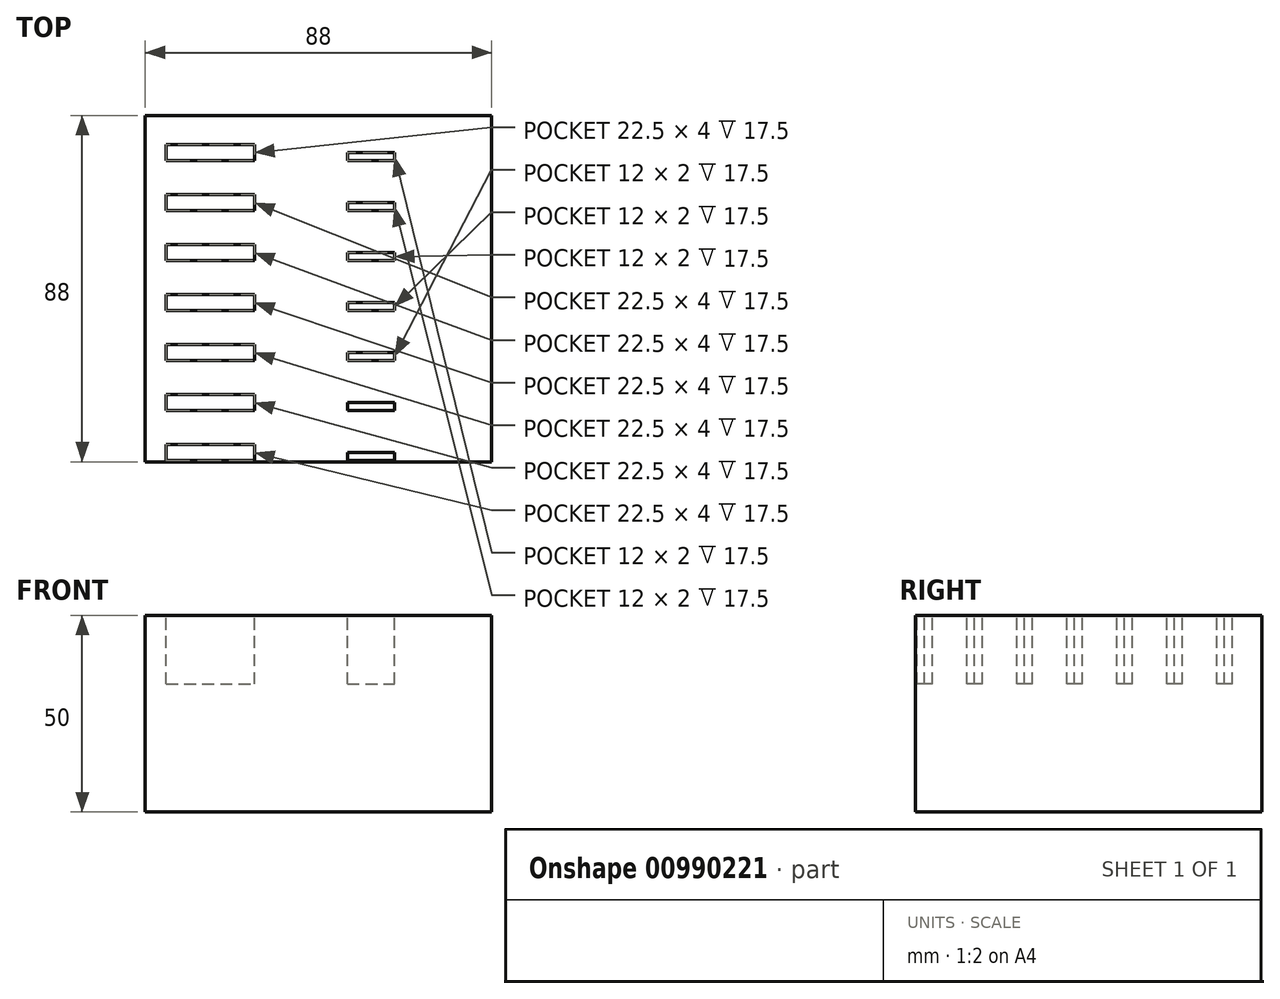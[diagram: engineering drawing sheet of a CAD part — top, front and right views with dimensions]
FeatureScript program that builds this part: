
annotation { "Feature Type Name" : "Feature", "Feature Type Description" : "" }
export const myFeature = defineFeature(function(context is Context, id is Id, definition is map)
    precondition{}
    {
        {
            var Q0;
            Q0=qCreatedBy(makeId("Top.planeOp"),FACE);
            var sketch = newSketch(context, id + "F0", { "sketchPlane" : qUnion([Q0])});
            skLineSegment(sketch, "E0.bottom", {"start": v(-39.99, 39.28) * mm, "end": v(48.01, 39.28) * mm});
            skLineSegment(sketch, "E0.top", {"start": v(-39.99, -48.72) * mm, "end": v(48.01, -48.72) * mm});
            skLineSegment(sketch, "E0.left", {"start": v(-39.99, 39.28) * mm, "end": v(-39.99, -48.72) * mm});
            skLineSegment(sketch, "E0.right", {"start": v(48.01, 39.28) * mm, "end": v(48.01, -48.72) * mm});
            skSolve(sketch);
        }
        {
            var Q0;
            Q0 = qSketchRegion(id + "F0", true);
            extrude(context, id + "F1", {"entities" : qUnion([Q0]), "depth" : 50 * mm, "offsetDistance" : 25.4 * mm});
        }
        {
            var Q0;
            Q0=makeQuery(id+"F1.opExtrude","CAP_FACE",FACE,{"disambiguationData":[OSD([sQuery(id+"F0.wireOp",EDGE,"E0.bottom"),sQuery(id+"F0.wireOp",EDGE,"E0.top"),sQuery(id+"F0.wireOp",EDGE,"E0.left"),sQuery(id+"F0.wireOp",EDGE,"E0.right")])],"isStart":false});
            var sketch = newSketch(context, id + "F2", { "sketchPlane" : qUnion([Q0])});
            skLineSegment(sketch, "E1.bottom", {"start": v(-34.7, 31.81) * mm, "end": v(-12.2, 31.81) * mm});
            skLineSegment(sketch, "E1.top", {"start": v(-34.7, 27.81) * mm, "end": v(-12.2, 27.81) * mm});
            skLineSegment(sketch, "E1.left", {"start": v(-34.7, 31.81) * mm, "end": v(-34.7, 27.81) * mm});
            skLineSegment(sketch, "E1.right", {"start": v(-12.2, 31.81) * mm, "end": v(-12.2, 27.81) * mm});
            skLineSegment(sketch, "E2.0.1.0", {"start": v(-34.7, 15.11) * mm, "end": v(-12.2, 15.11) * mm});
            skLineSegment(sketch, "E2.0.1.1", {"start": v(-34.7, 19.11) * mm, "end": v(-34.7, 15.11) * mm});
            skLineSegment(sketch, "E2.0.1.2", {"start": v(-34.7, 19.11) * mm, "end": v(-12.2, 19.11) * mm});
            skLineSegment(sketch, "E2.0.1.3", {"start": v(-12.2, 19.11) * mm, "end": v(-12.2, 15.11) * mm});
            skLineSegment(sketch, "E2.0.2.0", {"start": v(-34.7, 2.41) * mm, "end": v(-12.2, 2.41) * mm});
            skLineSegment(sketch, "E2.0.2.1", {"start": v(-34.7, 6.41) * mm, "end": v(-34.7, 2.41) * mm});
            skLineSegment(sketch, "E2.0.2.2", {"start": v(-34.7, 6.41) * mm, "end": v(-12.2, 6.41) * mm});
            skLineSegment(sketch, "E2.0.2.3", {"start": v(-12.2, 6.41) * mm, "end": v(-12.2, 2.41) * mm});
            skLineSegment(sketch, "E2.0.3.0", {"start": v(-34.7, -10.29) * mm, "end": v(-12.2, -10.29) * mm});
            skLineSegment(sketch, "E2.0.3.1", {"start": v(-34.7, -6.29) * mm, "end": v(-34.7, -10.29) * mm});
            skLineSegment(sketch, "E2.0.3.2", {"start": v(-34.7, -6.29) * mm, "end": v(-12.2, -6.29) * mm});
            skLineSegment(sketch, "E2.0.3.3", {"start": v(-12.2, -6.29) * mm, "end": v(-12.2, -10.29) * mm});
            skLineSegment(sketch, "E2.0.4.0", {"start": v(-34.7, -22.99) * mm, "end": v(-12.2, -22.99) * mm});
            skLineSegment(sketch, "E2.0.4.1", {"start": v(-34.7, -18.99) * mm, "end": v(-34.7, -22.99) * mm});
            skLineSegment(sketch, "E2.0.4.2", {"start": v(-34.7, -18.99) * mm, "end": v(-12.2, -18.99) * mm});
            skLineSegment(sketch, "E2.0.4.3", {"start": v(-12.2, -18.99) * mm, "end": v(-12.2, -22.99) * mm});
            skLineSegment(sketch, "E2.0.5.0", {"start": v(-34.7, -35.69) * mm, "end": v(-12.2, -35.69) * mm});
            skLineSegment(sketch, "E2.0.5.1", {"start": v(-34.7, -31.69) * mm, "end": v(-34.7, -35.69) * mm});
            skLineSegment(sketch, "E2.0.5.2", {"start": v(-34.7, -31.69) * mm, "end": v(-12.2, -31.69) * mm});
            skLineSegment(sketch, "E2.0.5.3", {"start": v(-12.2, -31.69) * mm, "end": v(-12.2, -35.69) * mm});
            skLineSegment(sketch, "E2.0.6.0", {"start": v(-34.7, -48.39) * mm, "end": v(-12.2, -48.39) * mm});
            skLineSegment(sketch, "E2.0.6.1", {"start": v(-34.7, -44.39) * mm, "end": v(-34.7, -48.39) * mm});
            skLineSegment(sketch, "E2.0.6.2", {"start": v(-34.7, -44.39) * mm, "end": v(-12.2, -44.39) * mm});
            skLineSegment(sketch, "E2.0.6.3", {"start": v(-12.2, -44.39) * mm, "end": v(-12.2, -48.39) * mm});
            skLineSegment(sketch, "E2.1.1.0", {"start": v(-34.7, 15.11) * mm, "end": v(-12.2, 15.11) * mm});
            skLineSegment(sketch, "E2.1.1.1", {"start": v(-34.7, 19.11) * mm, "end": v(-34.7, 15.11) * mm});
            skLineSegment(sketch, "E2.1.1.2", {"start": v(-34.7, 19.11) * mm, "end": v(-12.2, 19.11) * mm});
            skLineSegment(sketch, "E2.1.1.3", {"start": v(-12.2, 19.11) * mm, "end": v(-12.2, 15.11) * mm});
            skLineSegment(sketch, "E2.1.2.0", {"start": v(-34.7, 2.41) * mm, "end": v(-12.2, 2.41) * mm});
            skLineSegment(sketch, "E2.1.2.1", {"start": v(-34.7, 6.41) * mm, "end": v(-34.7, 2.41) * mm});
            skLineSegment(sketch, "E2.1.2.2", {"start": v(-34.7, 6.41) * mm, "end": v(-12.2, 6.41) * mm});
            skLineSegment(sketch, "E2.1.2.3", {"start": v(-12.2, 6.41) * mm, "end": v(-12.2, 2.41) * mm});
            skLineSegment(sketch, "E2.1.3.0", {"start": v(-34.7, -10.29) * mm, "end": v(-12.2, -10.29) * mm});
            skLineSegment(sketch, "E2.1.3.1", {"start": v(-34.7, -6.29) * mm, "end": v(-34.7, -10.29) * mm});
            skLineSegment(sketch, "E2.1.3.2", {"start": v(-34.7, -6.29) * mm, "end": v(-12.2, -6.29) * mm});
            skLineSegment(sketch, "E2.1.3.3", {"start": v(-12.2, -6.29) * mm, "end": v(-12.2, -10.29) * mm});
            skLineSegment(sketch, "E2.1.4.0", {"start": v(-34.7, -22.99) * mm, "end": v(-12.2, -22.99) * mm});
            skLineSegment(sketch, "E2.1.4.1", {"start": v(-34.7, -18.99) * mm, "end": v(-34.7, -22.99) * mm});
            skLineSegment(sketch, "E2.1.4.2", {"start": v(-34.7, -18.99) * mm, "end": v(-12.2, -18.99) * mm});
            skLineSegment(sketch, "E2.1.4.3", {"start": v(-12.2, -18.99) * mm, "end": v(-12.2, -22.99) * mm});
            skLineSegment(sketch, "E2.1.5.0", {"start": v(-34.7, -35.69) * mm, "end": v(-12.2, -35.69) * mm});
            skLineSegment(sketch, "E2.1.5.1", {"start": v(-34.7, -31.69) * mm, "end": v(-34.7, -35.69) * mm});
            skLineSegment(sketch, "E2.1.5.2", {"start": v(-34.7, -31.69) * mm, "end": v(-12.2, -31.69) * mm});
            skLineSegment(sketch, "E2.1.5.3", {"start": v(-12.2, -31.69) * mm, "end": v(-12.2, -35.69) * mm});
            skLineSegment(sketch, "E2.1.6.0", {"start": v(-34.7, -48.39) * mm, "end": v(-12.2, -48.39) * mm});
            skLineSegment(sketch, "E2.1.6.1", {"start": v(-34.7, -44.39) * mm, "end": v(-34.7, -48.39) * mm});
            skLineSegment(sketch, "E2.1.6.2", {"start": v(-34.7, -44.39) * mm, "end": v(-12.2, -44.39) * mm});
            skLineSegment(sketch, "E2.1.6.3", {"start": v(-12.2, -44.39) * mm, "end": v(-12.2, -48.39) * mm});
            skLineSegment(sketch, "E2.2.1.0", {"start": v(-34.7, 15.11) * mm, "end": v(-12.2, 15.11) * mm});
            skLineSegment(sketch, "E2.2.1.1", {"start": v(-34.7, 19.11) * mm, "end": v(-34.7, 15.11) * mm});
            skLineSegment(sketch, "E2.2.1.2", {"start": v(-34.7, 19.11) * mm, "end": v(-12.2, 19.11) * mm});
            skLineSegment(sketch, "E2.2.1.3", {"start": v(-12.2, 19.11) * mm, "end": v(-12.2, 15.11) * mm});
            skLineSegment(sketch, "E2.2.2.0", {"start": v(-34.7, 2.41) * mm, "end": v(-12.2, 2.41) * mm});
            skLineSegment(sketch, "E2.2.2.1", {"start": v(-34.7, 6.41) * mm, "end": v(-34.7, 2.41) * mm});
            skLineSegment(sketch, "E2.2.2.2", {"start": v(-34.7, 6.41) * mm, "end": v(-12.2, 6.41) * mm});
            skLineSegment(sketch, "E2.2.2.3", {"start": v(-12.2, 6.41) * mm, "end": v(-12.2, 2.41) * mm});
            skLineSegment(sketch, "E2.2.3.0", {"start": v(-34.7, -10.29) * mm, "end": v(-12.2, -10.29) * mm});
            skLineSegment(sketch, "E2.2.3.1", {"start": v(-34.7, -6.29) * mm, "end": v(-34.7, -10.29) * mm});
            skLineSegment(sketch, "E2.2.3.2", {"start": v(-34.7, -6.29) * mm, "end": v(-12.2, -6.29) * mm});
            skLineSegment(sketch, "E2.2.3.3", {"start": v(-12.2, -6.29) * mm, "end": v(-12.2, -10.29) * mm});
            skLineSegment(sketch, "E2.2.4.0", {"start": v(-34.7, -22.99) * mm, "end": v(-12.2, -22.99) * mm});
            skLineSegment(sketch, "E2.2.4.1", {"start": v(-34.7, -18.99) * mm, "end": v(-34.7, -22.99) * mm});
            skLineSegment(sketch, "E2.2.4.2", {"start": v(-34.7, -18.99) * mm, "end": v(-12.2, -18.99) * mm});
            skLineSegment(sketch, "E2.2.4.3", {"start": v(-12.2, -18.99) * mm, "end": v(-12.2, -22.99) * mm});
            skLineSegment(sketch, "E2.2.5.0", {"start": v(-34.7, -35.69) * mm, "end": v(-12.2, -35.69) * mm});
            skLineSegment(sketch, "E2.2.5.1", {"start": v(-34.7, -31.69) * mm, "end": v(-34.7, -35.69) * mm});
            skLineSegment(sketch, "E2.2.5.2", {"start": v(-34.7, -31.69) * mm, "end": v(-12.2, -31.69) * mm});
            skLineSegment(sketch, "E2.2.5.3", {"start": v(-12.2, -31.69) * mm, "end": v(-12.2, -35.69) * mm});
            skLineSegment(sketch, "E2.2.6.0", {"start": v(-34.7, -48.39) * mm, "end": v(-12.2, -48.39) * mm});
            skLineSegment(sketch, "E2.2.6.1", {"start": v(-34.7, -44.39) * mm, "end": v(-34.7, -48.39) * mm});
            skLineSegment(sketch, "E2.2.6.2", {"start": v(-34.7, -44.39) * mm, "end": v(-12.2, -44.39) * mm});
            skLineSegment(sketch, "E2.2.6.3", {"start": v(-12.2, -44.39) * mm, "end": v(-12.2, -48.39) * mm});
            skLineSegment(sketch, "E2.direction1", {"start": v(-34.7, 27.81) * mm, "end": v(-34.7, 27.81) * mm});
            skLineSegment(sketch, "E2.direction2", {"start": v(-34.7, 27.81) * mm, "end": v(-34.7, 15.11) * mm, "construction": true});
            skLineSegment(sketch, "E3.bottom", {"start": v(11.38, 29.81) * mm, "end": v(23.38, 29.81) * mm});
            skLineSegment(sketch, "E3.top", {"start": v(11.38, 27.81) * mm, "end": v(23.38, 27.81) * mm});
            skLineSegment(sketch, "E3.left", {"start": v(11.38, 29.81) * mm, "end": v(11.38, 27.81) * mm});
            skLineSegment(sketch, "E3.right", {"start": v(23.38, 29.81) * mm, "end": v(23.38, 27.81) * mm});
            skLineSegment(sketch, "E4", {"start": v(-12.2, 27.81) * mm, "end": v(11.38, 27.81) * mm, "construction": true});
            skLineSegment(sketch, "E5.0.1.0", {"start": v(11.38, 17.11) * mm, "end": v(23.38, 17.11) * mm});
            skLineSegment(sketch, "E5.0.1.1", {"start": v(11.38, 17.11) * mm, "end": v(11.38, 15.11) * mm});
            skLineSegment(sketch, "E5.0.1.2", {"start": v(11.38, 15.11) * mm, "end": v(23.38, 15.11) * mm});
            skLineSegment(sketch, "E5.0.1.3", {"start": v(23.38, 17.11) * mm, "end": v(23.38, 15.11) * mm});
            skLineSegment(sketch, "E5.0.2.0", {"start": v(11.38, 4.41) * mm, "end": v(23.38, 4.41) * mm});
            skLineSegment(sketch, "E5.0.2.1", {"start": v(11.38, 4.41) * mm, "end": v(11.38, 2.41) * mm});
            skLineSegment(sketch, "E5.0.2.2", {"start": v(11.38, 2.41) * mm, "end": v(23.38, 2.41) * mm});
            skLineSegment(sketch, "E5.0.2.3", {"start": v(23.38, 4.41) * mm, "end": v(23.38, 2.41) * mm});
            skLineSegment(sketch, "E5.0.3.0", {"start": v(11.38, -8.29) * mm, "end": v(23.38, -8.29) * mm});
            skLineSegment(sketch, "E5.0.3.1", {"start": v(11.38, -8.29) * mm, "end": v(11.38, -10.29) * mm});
            skLineSegment(sketch, "E5.0.3.2", {"start": v(11.38, -10.29) * mm, "end": v(23.38, -10.29) * mm});
            skLineSegment(sketch, "E5.0.3.3", {"start": v(23.38, -8.29) * mm, "end": v(23.38, -10.29) * mm});
            skLineSegment(sketch, "E5.0.4.0", {"start": v(11.38, -20.99) * mm, "end": v(23.38, -20.99) * mm});
            skLineSegment(sketch, "E5.0.4.1", {"start": v(11.38, -20.99) * mm, "end": v(11.38, -22.99) * mm});
            skLineSegment(sketch, "E5.0.4.2", {"start": v(11.38, -22.99) * mm, "end": v(23.38, -22.99) * mm});
            skLineSegment(sketch, "E5.0.4.3", {"start": v(23.38, -20.99) * mm, "end": v(23.38, -22.99) * mm});
            skLineSegment(sketch, "E5.0.5.0", {"start": v(11.38, -33.69) * mm, "end": v(23.38, -33.69) * mm});
            skLineSegment(sketch, "E5.0.5.1", {"start": v(11.38, -33.69) * mm, "end": v(11.38, -35.69) * mm});
            skLineSegment(sketch, "E5.0.5.2", {"start": v(11.38, -35.69) * mm, "end": v(23.38, -35.69) * mm});
            skLineSegment(sketch, "E5.0.5.3", {"start": v(23.38, -33.69) * mm, "end": v(23.38, -35.69) * mm});
            skLineSegment(sketch, "E5.0.6.0", {"start": v(11.38, -46.39) * mm, "end": v(23.38, -46.39) * mm});
            skLineSegment(sketch, "E5.0.6.1", {"start": v(11.38, -46.39) * mm, "end": v(11.38, -48.39) * mm});
            skLineSegment(sketch, "E5.0.6.2", {"start": v(11.38, -48.39) * mm, "end": v(23.38, -48.39) * mm});
            skLineSegment(sketch, "E5.0.6.3", {"start": v(23.38, -46.39) * mm, "end": v(23.38, -48.39) * mm});
            skLineSegment(sketch, "E5.1.1.0", {"start": v(11.38, 17.11) * mm, "end": v(23.38, 17.11) * mm});
            skLineSegment(sketch, "E5.1.1.1", {"start": v(11.38, 17.11) * mm, "end": v(11.38, 15.11) * mm});
            skLineSegment(sketch, "E5.1.1.2", {"start": v(11.38, 15.11) * mm, "end": v(23.38, 15.11) * mm});
            skLineSegment(sketch, "E5.1.1.3", {"start": v(23.38, 17.11) * mm, "end": v(23.38, 15.11) * mm});
            skLineSegment(sketch, "E5.1.2.0", {"start": v(11.38, 4.41) * mm, "end": v(23.38, 4.41) * mm});
            skLineSegment(sketch, "E5.1.2.1", {"start": v(11.38, 4.41) * mm, "end": v(11.38, 2.41) * mm});
            skLineSegment(sketch, "E5.1.2.2", {"start": v(11.38, 2.41) * mm, "end": v(23.38, 2.41) * mm});
            skLineSegment(sketch, "E5.1.2.3", {"start": v(23.38, 4.41) * mm, "end": v(23.38, 2.41) * mm});
            skLineSegment(sketch, "E5.1.3.0", {"start": v(11.38, -8.29) * mm, "end": v(23.38, -8.29) * mm});
            skLineSegment(sketch, "E5.1.3.1", {"start": v(11.38, -8.29) * mm, "end": v(11.38, -10.29) * mm});
            skLineSegment(sketch, "E5.1.3.2", {"start": v(11.38, -10.29) * mm, "end": v(23.38, -10.29) * mm});
            skLineSegment(sketch, "E5.1.3.3", {"start": v(23.38, -8.29) * mm, "end": v(23.38, -10.29) * mm});
            skLineSegment(sketch, "E5.1.4.0", {"start": v(11.38, -20.99) * mm, "end": v(23.38, -20.99) * mm});
            skLineSegment(sketch, "E5.1.4.1", {"start": v(11.38, -20.99) * mm, "end": v(11.38, -22.99) * mm});
            skLineSegment(sketch, "E5.1.4.2", {"start": v(11.38, -22.99) * mm, "end": v(23.38, -22.99) * mm});
            skLineSegment(sketch, "E5.1.4.3", {"start": v(23.38, -20.99) * mm, "end": v(23.38, -22.99) * mm});
            skLineSegment(sketch, "E5.1.5.0", {"start": v(11.38, -33.69) * mm, "end": v(23.38, -33.69) * mm});
            skLineSegment(sketch, "E5.1.5.1", {"start": v(11.38, -33.69) * mm, "end": v(11.38, -35.69) * mm});
            skLineSegment(sketch, "E5.1.5.2", {"start": v(11.38, -35.69) * mm, "end": v(23.38, -35.69) * mm});
            skLineSegment(sketch, "E5.1.5.3", {"start": v(23.38, -33.69) * mm, "end": v(23.38, -35.69) * mm});
            skLineSegment(sketch, "E5.1.6.0", {"start": v(11.38, -46.39) * mm, "end": v(23.38, -46.39) * mm});
            skLineSegment(sketch, "E5.1.6.1", {"start": v(11.38, -46.39) * mm, "end": v(11.38, -48.39) * mm});
            skLineSegment(sketch, "E5.1.6.2", {"start": v(11.38, -48.39) * mm, "end": v(23.38, -48.39) * mm});
            skLineSegment(sketch, "E5.1.6.3", {"start": v(23.38, -46.39) * mm, "end": v(23.38, -48.39) * mm});
            skLineSegment(sketch, "E5.2.1.0", {"start": v(11.38, 17.11) * mm, "end": v(23.38, 17.11) * mm});
            skLineSegment(sketch, "E5.2.1.1", {"start": v(11.38, 17.11) * mm, "end": v(11.38, 15.11) * mm});
            skLineSegment(sketch, "E5.2.1.2", {"start": v(11.38, 15.11) * mm, "end": v(23.38, 15.11) * mm});
            skLineSegment(sketch, "E5.2.1.3", {"start": v(23.38, 17.11) * mm, "end": v(23.38, 15.11) * mm});
            skLineSegment(sketch, "E5.2.2.0", {"start": v(11.38, 4.41) * mm, "end": v(23.38, 4.41) * mm});
            skLineSegment(sketch, "E5.2.2.1", {"start": v(11.38, 4.41) * mm, "end": v(11.38, 2.41) * mm});
            skLineSegment(sketch, "E5.2.2.2", {"start": v(11.38, 2.41) * mm, "end": v(23.38, 2.41) * mm});
            skLineSegment(sketch, "E5.2.2.3", {"start": v(23.38, 4.41) * mm, "end": v(23.38, 2.41) * mm});
            skLineSegment(sketch, "E5.2.3.0", {"start": v(11.38, -8.29) * mm, "end": v(23.38, -8.29) * mm});
            skLineSegment(sketch, "E5.2.3.1", {"start": v(11.38, -8.29) * mm, "end": v(11.38, -10.29) * mm});
            skLineSegment(sketch, "E5.2.3.2", {"start": v(11.38, -10.29) * mm, "end": v(23.38, -10.29) * mm});
            skLineSegment(sketch, "E5.2.3.3", {"start": v(23.38, -8.29) * mm, "end": v(23.38, -10.29) * mm});
            skLineSegment(sketch, "E5.2.4.0", {"start": v(11.38, -20.99) * mm, "end": v(23.38, -20.99) * mm});
            skLineSegment(sketch, "E5.2.4.1", {"start": v(11.38, -20.99) * mm, "end": v(11.38, -22.99) * mm});
            skLineSegment(sketch, "E5.2.4.2", {"start": v(11.38, -22.99) * mm, "end": v(23.38, -22.99) * mm});
            skLineSegment(sketch, "E5.2.4.3", {"start": v(23.38, -20.99) * mm, "end": v(23.38, -22.99) * mm});
            skLineSegment(sketch, "E5.2.5.0", {"start": v(11.38, -33.69) * mm, "end": v(23.38, -33.69) * mm});
            skLineSegment(sketch, "E5.2.5.1", {"start": v(11.38, -33.69) * mm, "end": v(11.38, -35.69) * mm});
            skLineSegment(sketch, "E5.2.5.2", {"start": v(11.38, -35.69) * mm, "end": v(23.38, -35.69) * mm});
            skLineSegment(sketch, "E5.2.5.3", {"start": v(23.38, -33.69) * mm, "end": v(23.38, -35.69) * mm});
            skLineSegment(sketch, "E5.2.6.0", {"start": v(11.38, -46.39) * mm, "end": v(23.38, -46.39) * mm});
            skLineSegment(sketch, "E5.2.6.1", {"start": v(11.38, -46.39) * mm, "end": v(11.38, -48.39) * mm});
            skLineSegment(sketch, "E5.2.6.2", {"start": v(11.38, -48.39) * mm, "end": v(23.38, -48.39) * mm});
            skLineSegment(sketch, "E5.2.6.3", {"start": v(23.38, -46.39) * mm, "end": v(23.38, -48.39) * mm});
            skLineSegment(sketch, "E5.direction1", {"start": v(11.38, 29.81) * mm, "end": v(11.38, 29.81) * mm});
            skLineSegment(sketch, "E5.direction2", {"start": v(11.38, 29.81) * mm, "end": v(11.38, 17.11) * mm, "construction": true});
            skSolve(sketch);
        }
        {
            var Q0;
            Q0 = qSketchRegion(id + "F2", true);
            extrude(context, id + "F3", {"entities" : qUnion([Q0]), "operationType" : NewBodyOperationType.REMOVE, "oppositeDirection" : true, "depth" : 17.5 * mm, "offsetDistance" : 25.4 * mm});
        }
    });
